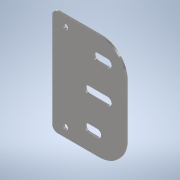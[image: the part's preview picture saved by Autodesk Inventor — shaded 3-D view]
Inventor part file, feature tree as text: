
AUTODESK INVENTOR PART (.ipt)
format: ipt  version: 2021 (Build 250183000, 183)  size: 503,296 bytes
history: native  units: mm
features: sketch x3, extrude x2, hole x2, fillet x2
ambient origin geometry x8: Origin, YZ Plane, XZ Plane, XY Plane, X Axis, Y Axis, Z Axis, Center Point
bodies: Solid1 (feature_tree)
feature tree (9):
  sketch  "Sketch1"  dims[d4=2190.0mm d5=3.0mm d6=0.0mm]
  extrude  "Extrusion1"  Depth=3.0mm TaperAngle=0.0deg
  hole  "Hole1"  [1 undecoded]
  extrude  "Extrusion2"  Depth=8.0mm
  hole  "Hole2"  [1 undecoded]
  fillet  "Fillet2"  Radius=30.0mm
  fillet  "Fillet3"  Radius=30.0mm
  sketch  "Sketch2"  dims[d10=50.0mm d11=50.0mm]
  sketch  "Sketch3"  dims[d12=12.0mm d13=6.0mm d14=4.0mm d15=2.0mm d16=90.0deg d17=8.0mm d18=20.594885mm d21=305.2mm d23=3.0mm d24=0.0mm d29=8.0mm d30=6.0mm d31=4.0mm d32=2.0mm d33=90.0deg d34=8.0mm d35=20.594885mm d36=30.0mm d37=30.0mm d38=27.5mm d39=55.0mm d49=40.0mm d50=8.0mm d51=20.0mm d52=14.0mm d53=14.0mm d54=20.0mm]
note: 2 required parameter values undecoded (feature->parameter linkage not recoverable at this tier; creation-order binding heuristic only, values carry confidence <= 0.55)
